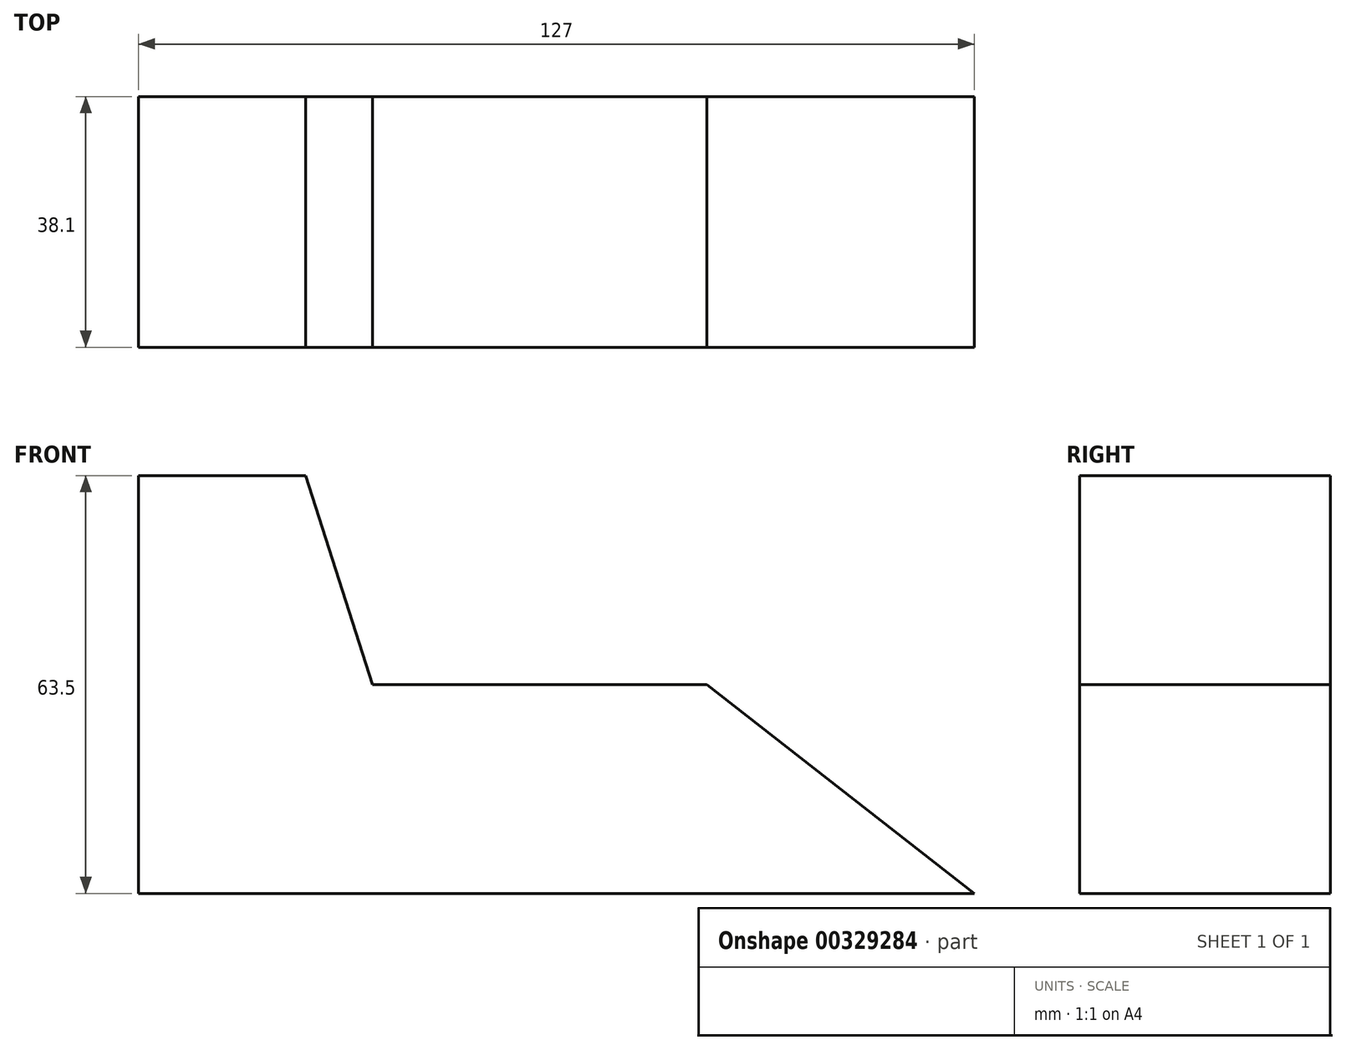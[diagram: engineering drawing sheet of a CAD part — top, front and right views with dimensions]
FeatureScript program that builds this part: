
annotation { "Feature Type Name" : "Feature", "Feature Type Description" : "" }
export const myFeature = defineFeature(function(context is Context, id is Id, definition is map)
    precondition{}
    {
        {
            var Q0;
            Q0=qCreatedBy(makeId("Front.planeOp"),FACE);
            var sketch = newSketch(context, id + "F0", { "sketchPlane" : qUnion([Q0])});
            skLineSegment(sketch, "E0", {"start": v(-60.93, -31.75) * mm, "end": v(66.07, -31.75) * mm});
            skLineSegment(sketch, "E1", {"start": v(-60.93, -31.75) * mm, "end": v(-60.93, 31.75) * mm});
            skLineSegment(sketch, "E2", {"start": v(-60.93, 31.75) * mm, "end": v(-35.53, 31.75) * mm});
            skLineSegment(sketch, "E3", {"start": v(-35.53, 31.75) * mm, "end": v(-25.36, 0) * mm});
            skLineSegment(sketch, "E4", {"start": v(-25.36, 0) * mm, "end": v(25.44, 0) * mm});
            skLineSegment(sketch, "E5", {"start": v(25.44, 0) * mm, "end": v(66.07, -31.75) * mm});
            skSolve(sketch);
        }
        {
            var Q0;
            Q0 = qSketchRegion(id + "F0", true);
            extrude(context, id + "F1", {"entities" : qUnion([Q0]), "depth" : 38.1 * mm});
        }
    });
